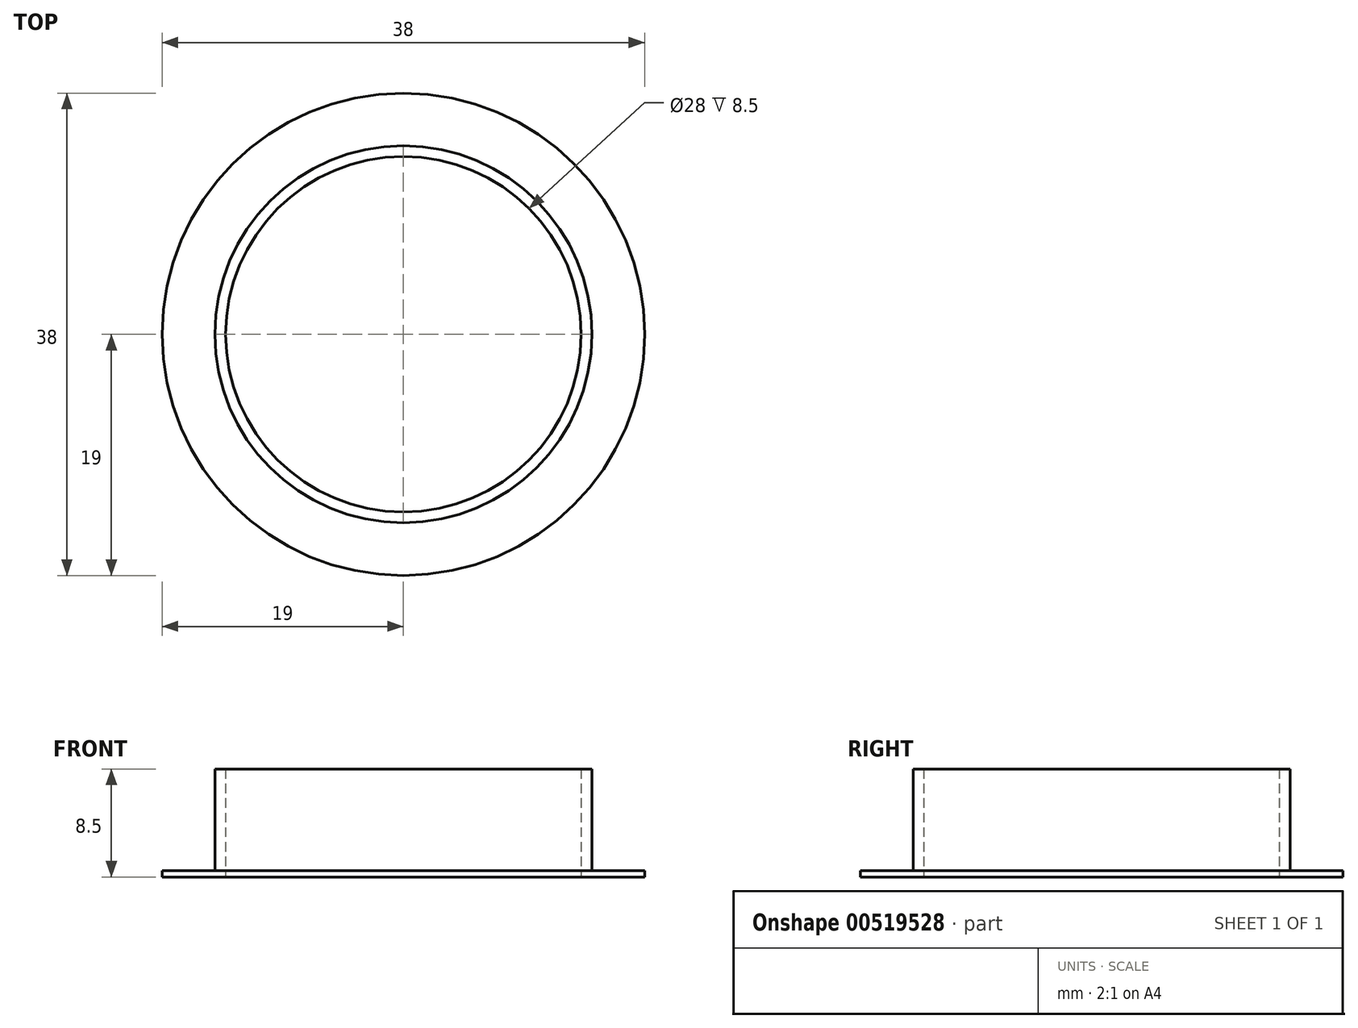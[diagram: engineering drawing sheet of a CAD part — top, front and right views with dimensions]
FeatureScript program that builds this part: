
annotation { "Feature Type Name" : "Feature", "Feature Type Description" : "" }
export const myFeature = defineFeature(function(context is Context, id is Id, definition is map)
    precondition{}
    {
        {
            var Q0;
            Q0=qCreatedBy(makeId("Top.planeOp"),FACE);
            var sketch = newSketch(context, id + "F0", { "sketchPlane" : qUnion([Q0])});
            skCircle(sketch, "E0", {"center": v(0, 0) * mm, "radius": 14 * mm});
            skCircle(sketch, "E1", {"center": v(0, 0) * mm, "radius": 14.85 * mm});
            skSolve(sketch);
        }
        {
            var Q0;
            Q0 = qSketchRegion(id + "F0", true);
            extrude(context, id + "F1", {"entities" : qUnion([Q0]), "depth" : 8 * mm, "offsetDistance" : 25 * mm});
        }
        {
            var Q0;
            Q0=qCreatedBy(makeId("Top.planeOp"),FACE);
            var sketch = newSketch(context, id + "F2", { "sketchPlane" : qUnion([Q0])});
            skCircle(sketch, "E2.0", {"center": v(0, 0) * mm, "radius": 14 * mm});
            skCircle(sketch, "E3", {"center": v(0, 0) * mm, "radius": 19 * mm});
            skSolve(sketch);
        }
        {
            var Q0;
            Q0=makeQuery(id+"F2.imprint","IMPRINT",FACE,{"disambiguationData":[TD([[makeQuery(id+"F2.imprint","IMPRINT",EDGE,{"derivedFrom":sQuery(id+"F2.wireOp",EDGE,"E2.0")}),-1.0]])]});
            extrude(context, id + "F3", {"entities" : qUnion([Q0]), "operationType" : NewBodyOperationType.ADD, "oppositeDirection" : true, "depth" : 0.5 * mm, "offsetDistance" : 25 * mm});
        }
    });
